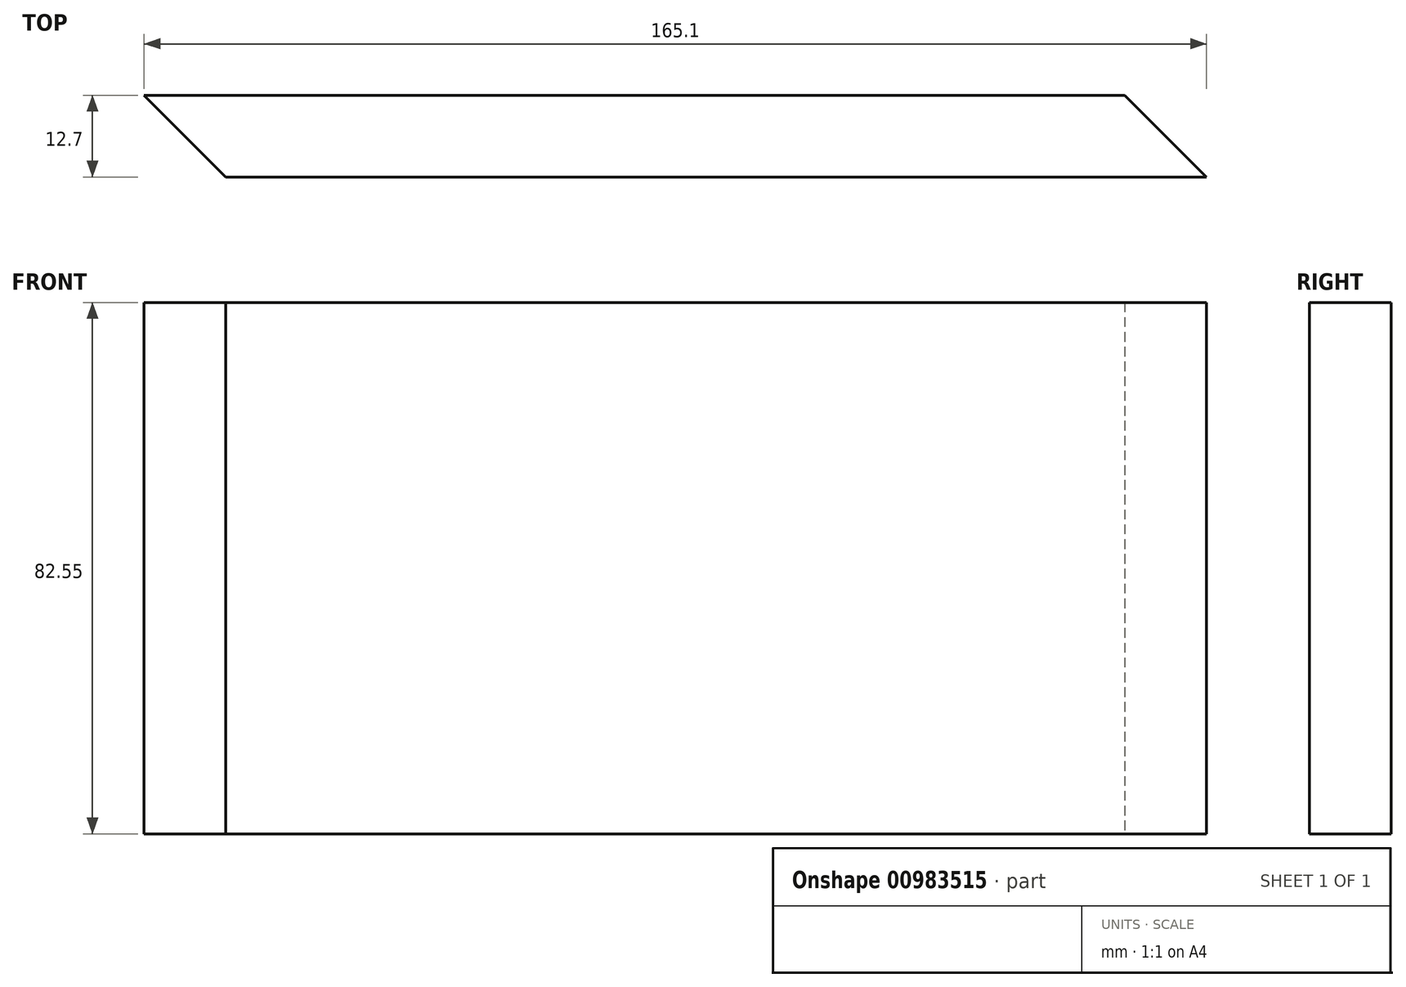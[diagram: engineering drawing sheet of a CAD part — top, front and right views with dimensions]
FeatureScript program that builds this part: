
annotation { "Feature Type Name" : "Feature", "Feature Type Description" : "" }
export const myFeature = defineFeature(function(context is Context, id is Id, definition is map)
    precondition{}
    {
        {
            var Q0;
            Q0=qCreatedBy(makeId("Front.planeOp"),FACE);
            var sketch = newSketch(context, id + "F0", { "sketchPlane" : qUnion([Q0])});
            skLineSegment(sketch, "E0.bottom", {"start": v(-100.53, 39.11) * mm, "end": v(64.57, 39.11) * mm});
            skLineSegment(sketch, "E0.top", {"start": v(-100.53, -43.44) * mm, "end": v(64.57, -43.44) * mm});
            skLineSegment(sketch, "E0.left", {"start": v(-100.53, 39.11) * mm, "end": v(-100.53, -43.44) * mm});
            skLineSegment(sketch, "E0.right", {"start": v(64.57, 39.11) * mm, "end": v(64.57, -43.44) * mm});
            skSolve(sketch);
        }
        {
            var Q0;
            Q0 = qSketchRegion(id + "F0", true);
            extrude(context, id + "F1", {"entities" : qUnion([Q0]), "depth" : 12.7 * mm, "offsetDistance" : 25.4 * mm});
        }
        {
            var Q0;
            Q0=makeQuery(id+"F1.opExtrude","CAP_EDGE",EDGE,{"disambiguationData":[OSD([sQuery(id+"F0.wireOp",EDGE,"E0.right")])],"isStart":true});
            var Q1;
            Q1=makeQuery(id+"F1.opExtrude","CAP_EDGE",EDGE,{"disambiguationData":[OSD([sQuery(id+"F0.wireOp",EDGE,"E0.left")])],"isStart":false});
            chamfer(context, id + "F2", {"entities" : qUnion([Q0, Q1]), "width" : 12.7 * mm, "tangentPropagation" : true});
        }
    });
